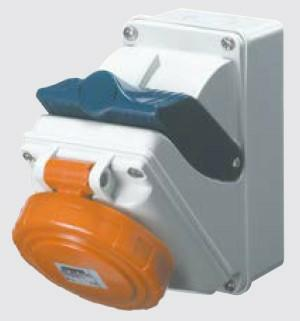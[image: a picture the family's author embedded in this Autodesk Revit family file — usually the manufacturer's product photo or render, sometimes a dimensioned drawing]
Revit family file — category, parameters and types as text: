
# Revit family: Building-IEC309Connections-GEWISS-COMBIBLOC-INTERLOCKED-SOCKET-OUTLETS_IP55
name_source: partatom
category: Apparecchi elettrici
units: mm (PartAtom-declared; Revit-internal decimal feet)

## family parameters
Condiviso = No
Host = Superficie
Mantenere orientamento annotazione = Sì
Punto di calcolo locali = Sì
Quota connettore circolare = Usa diametro
Taglio con vuoti quando caricato = No
Tipo di parte = Normale

## types (18) — shared parameters
BLOCCO = B=C
Catalogue = BUILDING
Electrocod = 2221
FORMULA = 1000 mm  [stored 3.28084 ft]
Frequency = 50/60 Hz
Glow wire test: = 850 °C (active parts) - 650 °C (passive parts)
IDF = 8df49ec9-f186-4604-9644-f3054fbccd40
IDT = 876c997d56934812acb3c8df0937ea93
IP degree = IP55
Immagine tipo = COMBIBLOC55Fondo.jpg
L = 155 mm
N.poli = 1
Operating temperature: = -25 +40 °C
POMELLO = bianco
PRESA = Giallo
Produttore = GEWISS S.p.A.
Prospetto di default = 1219 mm
Protection = NO (SBF)
SEO = Interlocked outlet
STRUTTURA = RAL - 7035
STRUTTURA ALTA = blue
Shock resistance = IK08
Spostamento_S = 1500 mm
Technical sheet = https://www.gewiss.com
Thermo-pressure with ball = 125 °C (active parts) - 80 °C (passive parts)
Typology = Compact
URL = https://www.gewiss.com
VETRO = Vetro
Version file RFA = 21.4
Voltaggio = 0 V
W = 115 mm
With back-mounting box = Yes

## per-type parameters (varying)
| type | Colour: | Descrizione | Modello | No. of poles | Rated current (A) | Rated voltage | Reference h |
| GW66449 - COMBIBLOC W.B.IP55 3P+E 16A 230V 9H | Blue | COMBIBLOC W.B.IP55 3P+E 16A 230V 9H | GW66449 | 3P+E | 16 | 200-250V | 9 |
| GW66448 - COMBIBLOC W.B.IP55 2P+E 16A 230V 6H | Blue | COMBIBLOC W.B.IP55 2P+E 16A 230V 6H | GW66448 | 2P+E | 16 | 200-250V | 6 |
| GW66462 - COMBIBLOC W.B.IP55 2P+E 32A 400V 9H | Red | COMBIBLOC W.B.IP55 2P+E 32A 400V 9H | GW66462 | 2P+E | 32 | 380-415V | 9 |
| GW66458 - COMBIBLOC W.B.IP55 3P+N+E 32A 110V 4H | Yellow | COMBIBLOC W.B.IP55 3P+N+E 32A 110V 4H | GW66458 | 3P+N+E | 32 | 100-130V | 4 |
| GW66450 - COMBIBLOC W.B.IP55 3P+N+E 16A 230V 9H | Blue | COMBIBLOC W.B.IP55 3P+N+E 16A 230V 9H | GW66450 | 3P+N+E | 16 | 200-250V | 9 |
| GW66460 - COMBIBLOC W.B.IP55 3P+E 32A 230V 9H | Blue | COMBIBLOC W.B.IP55 3P+E 32A 230V 9H | GW66460 | 3P+E | 32 | 200-250V | 9 |
| GW66464 - COMBIBLOC W.B.IP55 3P+N+E 32A 400V 6H | Red | COMBIBLOC W.B.IP55 3P+N+E 32A 400V 6H | GW66464 | 3P+N+E | 32 | 380-415V | 6 |
| GW66452 - COMBIBLOC W.B.IP55 3P+E 16A 400V 6H | Red | COMBIBLOC W.B.IP55 3P+E 16A 400V 6H | GW66452 | 3P+E | 16 | 380-415V | 6 |
| GW66463 - COMBIBLOC W.B.IP55 3P+E 32A 400V 6H | Red | COMBIBLOC W.B.IP55 3P+E 32A 400V 6H | GW66463 | 3P+E | 32 | 380-415V | 6 |
| GW66453 - COMBIBLOC W.B.IP55 3P+N+E 16A 400V 6H | Red | COMBIBLOC W.B.IP55 3P+N+E 16A 400V 6H | GW66453 | 3P+N+E | 16 | 380-415V | 6 |
| GW66456 - COMBIBLOC W.B.IP55 2P+E 32A 110V 4H | Yellow | COMBIBLOC W.B.IP55 2P+E 32A 110V 4H | GW66456 | 2P+E | 32 | 100-130V | 4 |
| GW66447 - COMBIBLOC W.B.IP55 3P+N+E 16A 110V 4H | Yellow | COMBIBLOC W.B.IP55 3P+N+E 16A 110V 4H | GW66447 | 3P+N+E | 16 | 100-130V | 4 |
| GW66461 - COMBIBLOC W.B.IP55 3P+N+E 32A 230V 9H | Blue | COMBIBLOC W.B.IP55 3P+N+E 32A 230V 9H | GW66461 | 3P+N+E | 32 | 200-250V | 9 |
| GW66445 - COMBIBLOC W.B.IP55 2P+E 16A 110V 4H | Yellow | COMBIBLOC W.B.IP55 2P+E 16A 110V 4H | GW66445 | 2P+E | 16 | 100-130V | 4 |
| GW66457 - COMBIBLOC W.B.IP55 3P+E 32A 110V 4H | Yellow | COMBIBLOC W.B.IP55 3P+E 32A 110V 4H | GW66457 | 3P+E | 32 | 100-130V | 4 |
| GW66459 - COMBIBLOC W.B.IP55 2P+E 32A 230V 6H | Blue | COMBIBLOC W.B.IP55 2P+E 32A 230V 6H | GW66459 | 2P+E | 32 | 200-250V | 6 |
| GW66451 - COMBIBLOC W.B.IP55 2P+E 16A 400V 9H | Red | COMBIBLOC W.B.IP55 2P+E 16A 400V 9H | GW66451 | 2P+E | 16 | 380-415V | 9 |
| GW66446 - COMBIBLOC W.B.IP55 3P+E 16A 110V 4H | Yellow | COMBIBLOC W.B.IP55 3P+E 16A 110V 4H | GW66446 | 3P+E | 16 | 100-130V | 4 |

note: [stored X ft] marks values corroborated as IEEE doubles in the binary element streams (Revit-internal decimal feet)

## geometry (parser evidence)
native form markers: Sweep x4
no freeform markers — native parametric forms only
